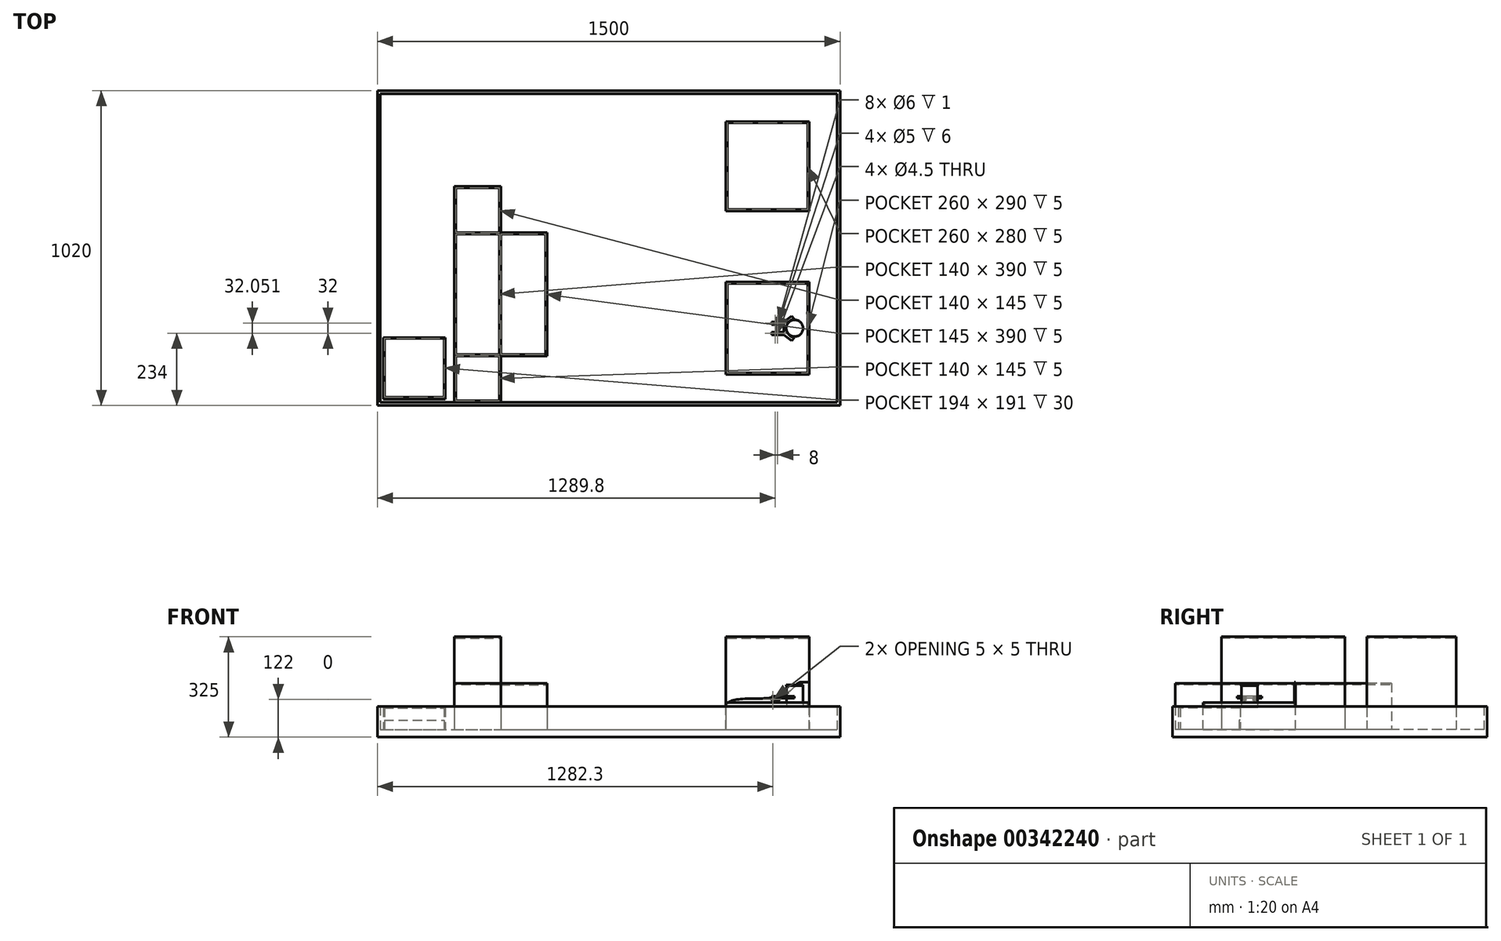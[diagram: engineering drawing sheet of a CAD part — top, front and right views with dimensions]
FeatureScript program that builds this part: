
annotation { "Feature Type Name" : "Feature", "Feature Type Description" : "" }
export const myFeature = defineFeature(function(context is Context, id is Id, definition is map)
    precondition{}
    {
        {
            var Q0;
            Q0=qCreatedBy(makeId("Top.planeOp"),FACE);
            var sketch = newSketch(context, id + "F0", { "sketchPlane" : qUnion([Q0])});
            skCircle(sketch, "E0", {"center": v(0, 0) * mm, "radius": 27.2 * mm});
            skSolve(sketch);
        }
        {
            var Q0;
            Q0=qSketchRegion(id+"F0",true);
            extrude(context, id + "F1", {"entities" : qUnion([Q0]), "depth" : 2.83 * mm});
        }
        {
            var Q0;
            Q0=makeQuery(id+"F1.opExtrude","CAP_FACE",FACE,{"disambiguationData":[OSD([sQuery(id+"F0.wireOp",EDGE,"E0")])],"isStart":false});
            var sketch = newSketch(context, id + "F2", { "sketchPlane" : qUnion([Q0])});
            skCircle(sketch, "E1", {"center": v(0, 0) * mm, "radius": 26.4 * mm});
            skSolve(sketch);
        }
        {
            var Q0;
            Q0=qSketchRegion(id+"F2",true);
            extrude(context, id + "F3", {"entities" : qUnion([Q0]), "operationType" : NewBodyOperationType.ADD, "depth" : 67.36 * mm});
        }
        {
            var Q0;
            Q0=makeQuery(id+"F3.opExtrude","CAP_FACE",FACE,{"disambiguationData":[OSD([sQuery(id+"F2.wireOp",EDGE,"E1")])],"isStart":false});
            var sketch = newSketch(context, id + "F4", { "sketchPlane" : qUnion([Q0])});
            skCircle(sketch, "E2", {"center": v(0, 0) * mm, "radius": 27.2 * mm});
            skSolve(sketch);
        }
        {
            var Q0;
            Q0=qSketchRegion(id+"F4",true);
            extrude(context, id + "F5", {"entities" : qUnion([Q0]), "operationType" : NewBodyOperationType.ADD, "depth" : 2.83 * mm});
        }
        {
            var Q0;
            Q0=makeQuery(id+"F5.opExtrude","CAP_FACE",FACE,{"disambiguationData":[OSD([sQuery(id+"F4.wireOp",EDGE,"E2")])],"isStart":false});
            var sketch = newSketch(context, id + "F6", { "sketchPlane" : qUnion([Q0])});
            skSolve(sketch);
        }
        {
            var Q0;
            Q0=qCreatedBy(makeId("Top.planeOp"),FACE);
            cPlane(context, id + "F7", {"entities" : qUnion([Q0]), "cplaneType" : CPlaneType.OFFSET, "offset" : 25 * mm, "width" : 150 * mm, "height" : 150 * mm});
        }
        {
            var Q0;
            Q0=makeQuery(id+"F6.imprint","IMPRINT",FACE,{"disambiguationData":[TD([[makeQuery(id+"F6.imprint","IMPRINT",EDGE,{"derivedFrom":makeQuery(id+"F5.opExtrude","CAP_EDGE",EDGE,{"disambiguationData":[OSD([sQuery(id+"F4.wireOp",EDGE,"E2")])],"isStart":false})}),1.0]])]});
            var sketch = newSketch(context, id + "F8", { "sketchPlane" : qUnion([Q0])});
            skSolve(sketch);
        }
        {
            var Q0;
            Q0=qCreatedBy(makeId("Top.planeOp"),FACE);
            var sketch = newSketch(context, id + "F9", { "sketchPlane" : qUnion([Q0])});
            skLineSegment(sketch, "E3.bottom", {"start": v(-222.8, -150) * mm, "end": v(47.2, -150) * mm});
            skLineSegment(sketch, "E3.top", {"start": v(-222.8, 150) * mm, "end": v(47.2, 150) * mm});
            skLineSegment(sketch, "E3.left", {"start": v(-222.8, -150) * mm, "end": v(-222.8, 150) * mm});
            skLineSegment(sketch, "E3.right", {"start": v(47.2, -150) * mm, "end": v(47.2, 150) * mm});
            skSolve(sketch);
        }
        {
            var Q0;
            Q0=qSketchRegion(id+"F9",true);
            extrude(context, id + "F10", {"entities" : qUnion([Q0]), "oppositeDirection" : true, "depth" : 72 * mm});
        }
        {
            var Q0;
            Q0=makeQuery(id+"F10.opExtrude","CAP_FACE",FACE,{"disambiguationData":[OSD([sQuery(id+"F9.wireOp",EDGE,"E3.bottom"),sQuery(id+"F9.wireOp",EDGE,"E3.top"),sQuery(id+"F9.wireOp",EDGE,"E3.left"),sQuery(id+"F9.wireOp",EDGE,"E3.right")])],"isStart":true});
            var sketch = newSketch(context, id + "F11", { "sketchPlane" : qUnion([Q0])});
            skLineSegment(sketch, "E4.bottom", {"start": v(-222.8, -150) * mm, "end": v(47.2, -150) * mm});
            skLineSegment(sketch, "E4.top", {"start": v(-222.8, -145) * mm, "end": v(42.2, -145) * mm});
            skLineSegment(sketch, "E4.left", {"start": v(-222.8, -150) * mm, "end": v(-222.8, -145) * mm});
            skLineSegment(sketch, "E5.bottom", {"start": v(47.2, 150) * mm, "end": v(42.2, 150) * mm});
            skLineSegment(sketch, "E5.left", {"start": v(47.2, 150) * mm, "end": v(47.2, -150) * mm});
            skLineSegment(sketch, "E5.right", {"start": v(42.2, 150) * mm, "end": v(42.2, -145) * mm});
            skSolve(sketch);
        }
        {
            var Q0;
            Q0=qSketchRegion(id+"F11",true);
            extrude(context, id + "F12", {"entities" : qUnion([Q0]), "operationType" : NewBodyOperationType.ADD, "depth" : 15 * mm});
        }
        {
            var Q0;
            Q0=makeQuery(id+"F12.boolean.opBoolean","MERGE",FACE,{"derivedFrom":[makeQuery(id+"F10.opExtrude","SWEPT_FACE",FACE,{"disambiguationData":[OSD([sQuery(id+"F9.wireOp",EDGE,"E3.top")])]}),makeQuery(id+"F12.opExtrude","SWEPT_FACE",FACE,{"disambiguationData":[OSD([sQuery(id+"F11.wireOp",EDGE,"E5.bottom")])]})]});
            var sketch = newSketch(context, id + "F13", { "sketchPlane" : qUnion([Q0])});
            skLineSegment(sketch, "E6", {"start": v(-47.2, 81.36) * mm, "end": v(-21.31, 81.36) * mm});
            skFitSpline(sketch, "E7", {"points": [v(-21.31, 81.36) * mm, v(15.24, 52.01) * mm, v(114.14, 28.17) * mm, v(222.8, 0) * mm], "startDerivative": vector(181.02, 0.3) * mm, "endDerivative": vector(-1.73, -239.85) * mm});
            skLineSegment(sketch, "E8", {"start": v(-47.2, 81.36) * mm, "end": v(-47.2, -72) * mm});
            skLineSegment(sketch, "E9", {"start": v(-47.2, -72) * mm, "end": v(222.8, -72) * mm});
            skLineSegment(sketch, "E10", {"start": v(222.8, -72) * mm, "end": v(222.8, 0) * mm});
            skSolve(sketch);
        }
        {
            var Q0;
            Q0=qSketchRegion(id+"F13",true);
            extrude(context, id + "F14", {"entities" : qUnion([Q0]), "operationType" : NewBodyOperationType.ADD, "oppositeDirection" : true, "depth" : 5 * mm});
        }
        {
            var Q0;
            Q0=makeQuery(id+"F10.opExtrude","CAP_FACE",FACE,{"disambiguationData":[OSD([sQuery(id+"F9.wireOp",EDGE,"E3.bottom"),sQuery(id+"F9.wireOp",EDGE,"E3.top"),sQuery(id+"F9.wireOp",EDGE,"E3.left"),sQuery(id+"F9.wireOp",EDGE,"E3.right")])],"isStart":true});
            var sketch = newSketch(context, id + "F15", { "sketchPlane" : qUnion([Q0])});
            skLineSegment(sketch, "E11.bottom", {"start": v(-222.8, 145) * mm, "end": v(-217.8, 145) * mm});
            skLineSegment(sketch, "E11.top", {"start": v(-222.8, -145) * mm, "end": v(-217.8, -145) * mm});
            skLineSegment(sketch, "E11.left", {"start": v(-222.8, 145) * mm, "end": v(-222.8, -145) * mm});
            skLineSegment(sketch, "E11.right", {"start": v(-217.8, 145) * mm, "end": v(-217.8, -145) * mm});
            skSolve(sketch);
        }
        {
            var Q0;
            Q0=qSketchRegion(id+"F15",true);
            extrude(context, id + "F16", {"entities" : qUnion([Q0]), "operationType" : NewBodyOperationType.ADD, "depth" : 5 * mm});
        }
        {
            var Q0;
            Q0=makeQuery(id+"F10.opExtrude","CAP_FACE",FACE,{"disambiguationData":[OSD([sQuery(id+"F9.wireOp",EDGE,"E3.bottom"),sQuery(id+"F9.wireOp",EDGE,"E3.top"),sQuery(id+"F9.wireOp",EDGE,"E3.left"),sQuery(id+"F9.wireOp",EDGE,"E3.right")])],"isStart":false});
            var sketch = newSketch(context, id + "F17", { "sketchPlane" : qUnion([Q0])});
            skLineSegment(sketch, "E12.bottom", {"start": v(147.2, 250) * mm, "end": v(-1352.8, 250) * mm});
            skLineSegment(sketch, "E12.top", {"start": v(147.2, -770) * mm, "end": v(-1352.8, -770) * mm});
            skLineSegment(sketch, "E12.left", {"start": v(147.2, 250) * mm, "end": v(147.2, -770) * mm});
            skLineSegment(sketch, "E12.right", {"start": v(-1352.8, 250) * mm, "end": v(-1352.8, -770) * mm});
            skSolve(sketch);
        }
        {
            var Q0;
            Q0=qSketchRegion(id+"F17",true);
            extrude(context, id + "F18", {"entities" : qUnion([Q0]), "operationType" : NewBodyOperationType.ADD, "depth" : 25 * mm});
        }
        {
            var Q0;
            Q0=makeQuery(id+"F18.opExtrude","CAP_FACE",FACE,{"disambiguationData":[OSD([sQuery(id+"F17.wireOp",EDGE,"E12.bottom"),sQuery(id+"F17.wireOp",EDGE,"E12.top"),sQuery(id+"F17.wireOp",EDGE,"E12.left"),sQuery(id+"F17.wireOp",EDGE,"E12.right")])],"isStart":true});
            var sketch = newSketch(context, id + "F19", { "sketchPlane" : qUnion([Q0])});
            skLineSegment(sketch, "E13.bottom", {"start": v(-222.8, 670) * mm, "end": v(47.2, 670) * mm});
            skLineSegment(sketch, "E13.top", {"start": v(-222.8, 380) * mm, "end": v(47.2, 380) * mm});
            skLineSegment(sketch, "E13.left", {"start": v(-222.8, 670) * mm, "end": v(-222.8, 380) * mm});
            skLineSegment(sketch, "E13.right", {"start": v(47.2, 670) * mm, "end": v(47.2, 380) * mm});
            skSolve(sketch);
        }
        {
            var Q0;
            Q0=qSketchRegion(id+"F19",true);
            extrude(context, id + "F20", {"entities" : qUnion([Q0]), "operationType" : NewBodyOperationType.ADD, "depth" : 300 * mm});
        }
        {
            var Q0;
            Q0=makeQuery(id+"F20.opExtrude","CAP_FACE",FACE,{"disambiguationData":[OSD([sQuery(id+"F19.wireOp",EDGE,"E13.bottom"),sQuery(id+"F19.wireOp",EDGE,"E13.top"),sQuery(id+"F19.wireOp",EDGE,"E13.left"),sQuery(id+"F19.wireOp",EDGE,"E13.right")])],"isStart":false});
            var sketch = newSketch(context, id + "F21", { "sketchPlane" : qUnion([Q0])});
            skLineSegment(sketch, "E14.bottom", {"start": v(-217.8, 665) * mm, "end": v(42.2, 665) * mm});
            skLineSegment(sketch, "E14.top", {"start": v(-217.8, 385) * mm, "end": v(42.2, 385) * mm});
            skLineSegment(sketch, "E14.left", {"start": v(-217.8, 665) * mm, "end": v(-217.8, 385) * mm});
            skLineSegment(sketch, "E14.right", {"start": v(42.2, 665) * mm, "end": v(42.2, 385) * mm});
            skSolve(sketch);
        }
        {
            var Q0;
            Q0=qSketchRegion(id+"F21",true);
            extrude(context, id + "F22", {"entities" : qUnion([Q0]), "operationType" : NewBodyOperationType.REMOVE, "oppositeDirection" : true, "depth" : 5 * mm});
        }
        {
            var Q0;
            Q0=makeQuery(id+"F18.opExtrude","CAP_FACE",FACE,{"disambiguationData":[OSD([sQuery(id+"F17.wireOp",EDGE,"E12.bottom"),sQuery(id+"F17.wireOp",EDGE,"E12.top"),sQuery(id+"F17.wireOp",EDGE,"E12.left"),sQuery(id+"F17.wireOp",EDGE,"E12.right")])],"isStart":true});
            var sketch = newSketch(context, id + "F23", { "sketchPlane" : qUnion([Q0])});
            skLineSegment(sketch, "E15.bottom", {"start": v(-1352.8, 770) * mm, "end": v(147.2, 770) * mm});
            skLineSegment(sketch, "E15.top", {"start": v(-1352.8, -250) * mm, "end": v(147.2, -250) * mm});
            skLineSegment(sketch, "E15.left", {"start": v(-1352.8, 770) * mm, "end": v(-1352.8, -250) * mm});
            skLineSegment(sketch, "E15.right", {"start": v(147.2, 770) * mm, "end": v(147.2, -250) * mm});
            skLineSegment(sketch, "E16.bottom", {"start": v(-1342.8, 760) * mm, "end": v(137.2, 760) * mm});
            skLineSegment(sketch, "E16.top", {"start": v(-1342.8, -240) * mm, "end": v(137.2, -240) * mm});
            skLineSegment(sketch, "E16.left", {"start": v(-1342.8, 760) * mm, "end": v(-1342.8, -240) * mm});
            skLineSegment(sketch, "E16.right", {"start": v(137.2, 760) * mm, "end": v(137.2, -240) * mm});
            skSolve(sketch);
        }
        {
            var Q0;
            Q0=qSketchRegion(id+"F23",true);
            extrude(context, id + "F24", {"entities" : qUnion([Q0]), "operationType" : NewBodyOperationType.ADD, "depth" : 75 * mm});
        }
        {
            var Q0;
            Q0=makeQuery(id+"F18.opExtrude","CAP_FACE",FACE,{"disambiguationData":[OSD([sQuery(id+"F17.wireOp",EDGE,"E12.bottom"),sQuery(id+"F17.wireOp",EDGE,"E12.top"),sQuery(id+"F17.wireOp",EDGE,"E12.left"),sQuery(id+"F17.wireOp",EDGE,"E12.right")])],"isStart":true});
            var sketch = newSketch(context, id + "F25", { "sketchPlane" : qUnion([Q0])});
            skLineSegment(sketch, "E17.bottom", {"start": v(-1102.8, 460) * mm, "end": v(-952.8, 460) * mm});
            skLineSegment(sketch, "E17.top", {"start": v(-1102.8, -240) * mm, "end": v(-952.8, -240) * mm});
            skLineSegment(sketch, "E17.left", {"start": v(-1102.8, 460) * mm, "end": v(-1102.8, -240) * mm});
            skLineSegment(sketch, "E17.right", {"start": v(-952.8, 460) * mm, "end": v(-952.8, 310) * mm});
            skLineSegment(sketch, "E18.bottom", {"start": v(-952.8, 310) * mm, "end": v(-802.8, 310) * mm});
            skLineSegment(sketch, "E18.top", {"start": v(-952.8, -90) * mm, "end": v(-802.8, -90) * mm});
            skLineSegment(sketch, "E18.right", {"start": v(-802.8, 310) * mm, "end": v(-802.8, -90) * mm});
            skLineSegment(sketch, "E19.trimOffspring", {"start": v(-952.8, -90) * mm, "end": v(-952.8, -240) * mm});
            skSolve(sketch);
        }
        {
            var Q0;
            Q0=qSketchRegion(id+"F25",true);
            extrude(context, id + "F26", {"entities" : qUnion([Q0]), "operationType" : NewBodyOperationType.ADD, "depth" : 150 * mm});
        }
        {
            var Q0;
            Q0=makeQuery(id+"F26.opExtrude","CAP_FACE",FACE,{"disambiguationData":[OSD([sQuery(id+"F25.wireOp",EDGE,"E17.bottom"),sQuery(id+"F25.wireOp",EDGE,"E17.top"),sQuery(id+"F25.wireOp",EDGE,"E17.left"),sQuery(id+"F25.wireOp",EDGE,"E17.right"),sQuery(id+"F25.wireOp",EDGE,"E18.bottom"),sQuery(id+"F25.wireOp",EDGE,"E18.top"),sQuery(id+"F25.wireOp",EDGE,"E18.right"),sQuery(id+"F25.wireOp",EDGE,"E19.trimOffspring")])],"isStart":false});
            var sketch = newSketch(context, id + "F27", { "sketchPlane" : qUnion([Q0])});
            skLineSegment(sketch, "E20.bottom", {"start": v(-952.8, 310) * mm, "end": v(-1102.8, 310) * mm});
            skLineSegment(sketch, "E20.top", {"start": v(-952.8, -90) * mm, "end": v(-1102.8, -90) * mm});
            skLineSegment(sketch, "E20.left", {"start": v(-952.8, 310) * mm, "end": v(-952.8, -90) * mm});
            skLineSegment(sketch, "E20.right", {"start": v(-1102.8, 310) * mm, "end": v(-1102.8, -90) * mm});
            skSolve(sketch);
        }
        {
            var Q0;
            Q0=qSketchRegion(id+"F27",true);
            extrude(context, id + "F28", {"entities" : qUnion([Q0]), "operationType" : NewBodyOperationType.ADD, "depth" : 150 * mm});
        }
        {
            var Q0;
            Q0=makeQuery(id+"F28.opExtrude","CAP_FACE",FACE,{"disambiguationData":[OSD([sQuery(id+"F27.wireOp",EDGE,"E20.bottom"),sQuery(id+"F27.wireOp",EDGE,"E20.top"),sQuery(id+"F27.wireOp",EDGE,"E20.left"),sQuery(id+"F27.wireOp",EDGE,"E20.right")])],"isStart":false});
            var sketch = newSketch(context, id + "F29", { "sketchPlane" : qUnion([Q0])});
            skLineSegment(sketch, "E21.bottom", {"start": v(-1097.8, 305) * mm, "end": v(-957.8, 305) * mm});
            skLineSegment(sketch, "E21.top", {"start": v(-1097.8, -85) * mm, "end": v(-957.8, -85) * mm});
            skLineSegment(sketch, "E21.left", {"start": v(-1097.8, 305) * mm, "end": v(-1097.8, -85) * mm});
            skLineSegment(sketch, "E21.right", {"start": v(-957.8, 305) * mm, "end": v(-957.8, -85) * mm});
            skSolve(sketch);
        }
        {
            var Q0;
            Q0=qSketchRegion(id+"F29",true);
            extrude(context, id + "F30", {"entities" : qUnion([Q0]), "operationType" : NewBodyOperationType.REMOVE, "oppositeDirection" : true, "depth" : 5 * mm});
        }
        {
            var Q0;
            {var subQ0=sQuery(id+"F25.wireOp",EDGE,"E17.left");var subQ1=sQuery(id+"F25.wireOp",EDGE,"E18.bottom");var subQ2=sQuery(id+"F25.wireOp",EDGE,"E17.right");var subQ3=sQuery(id+"F25.wireOp",EDGE,"E17.bottom");var subQ4=makeQuery(id+"F26.opExtrude","CAP_FACE",FACE,{"disambiguationData":[OSD([subQ3,sQuery(id+"F25.wireOp",EDGE,"E17.top"),subQ0,subQ2,subQ1,sQuery(id+"F25.wireOp",EDGE,"E18.top"),sQuery(id+"F25.wireOp",EDGE,"E18.right"),sQuery(id+"F25.wireOp",EDGE,"E19.trimOffspring")])],"isStart":false});Q0=makeQuery(id+"F28.boolean.opBoolean","SPLIT",FACE,{"disambiguationData":[TD([makeQuery(id+"F26.opExtrude","SWEPT_FACE",FACE,{"disambiguationData":[OSD([subQ3])]})])],"derivedFrom":subQ4});}
            var sketch = newSketch(context, id + "F31", { "sketchPlane" : qUnion([Q0])});
            skLineSegment(sketch, "E22.bottom", {"start": v(-1097.8, 455) * mm, "end": v(-957.8, 455) * mm});
            skLineSegment(sketch, "E22.top", {"start": v(-1097.8, 310) * mm, "end": v(-957.8, 310) * mm});
            skLineSegment(sketch, "E22.left", {"start": v(-1097.8, 455) * mm, "end": v(-1097.8, 310) * mm});
            skLineSegment(sketch, "E22.right", {"start": v(-957.8, 455) * mm, "end": v(-957.8, 310) * mm});
            skLineSegment(sketch, "E23.bottom", {"start": v(-952.8, 305) * mm, "end": v(-807.8, 305) * mm});
            skLineSegment(sketch, "E23.top", {"start": v(-952.8, -85) * mm, "end": v(-807.8, -85) * mm});
            skLineSegment(sketch, "E23.left", {"start": v(-952.8, 305) * mm, "end": v(-952.8, -85) * mm});
            skLineSegment(sketch, "E23.right", {"start": v(-807.8, 305) * mm, "end": v(-807.8, -85) * mm});
            skLineSegment(sketch, "E24.bottom", {"start": v(-1097.8, -90) * mm, "end": v(-957.8, -90) * mm});
            skLineSegment(sketch, "E24.top", {"start": v(-1097.8, -235) * mm, "end": v(-957.8, -235) * mm});
            skLineSegment(sketch, "E24.left", {"start": v(-1097.8, -90) * mm, "end": v(-1097.8, -235) * mm});
            skLineSegment(sketch, "E24.right", {"start": v(-957.8, -90) * mm, "end": v(-957.8, -235) * mm});
            skSolve(sketch);
        }
        {
            var Q0;
            Q0=qSketchRegion(id+"F31",true);
            extrude(context, id + "F32", {"entities" : qUnion([Q0]), "operationType" : NewBodyOperationType.REMOVE, "oppositeDirection" : true, "depth" : 5 * mm});
        }
        {
            var Q0;
            Q0=qCreatedBy(id+"F7.planeOp",FACE);
            var sketch = newSketch(context, id + "F33", { "sketchPlane" : qUnion([Q0])});
            skLineSegment(sketch, "E25", {"start": v(0, 0) * mm, "end": v(-90, 0) * mm, "construction": true});
            skLineSegment(sketch, "E26.bottom", {"start": v(-74.5, -12) * mm, "end": v(-55, -12) * mm});
            skLineSegment(sketch, "E26.top", {"start": v(-74.5, -20) * mm, "end": v(-55, -20) * mm});
            skLineSegment(sketch, "E26.left", {"start": v(-74.5, -12) * mm, "end": v(-74.5, -13) * mm});
            skPoint(sketch, "E27.visualSharp", {"position": v(-51, -12) * mm});
            skPoint(sketch, "E28.visualSharp", {"position": v(-51, -20) * mm});
            skCircle(sketch, "E29", {"center": v(-55, -16) * mm, "radius": 3 * mm});
            skLineSegment(sketch, "E30", {"start": v(-59, -3.98) * mm, "end": v(-59, -18.08) * mm, "construction": true});
            skCircle(sketch, "E31.MirrorC", {"center": v(-63, -16) * mm, "radius": 3 * mm});
            skLineSegment(sketch, "E32.bottom", {"start": v(-74.5, -13) * mm, "end": v(-65.65, -13) * mm});
            skLineSegment(sketch, "E32.top", {"start": v(-74.5, -19) * mm, "end": v(-65.65, -19) * mm});
            skArc(sketch, "E33", {"start": v(-65.65, -13) * mm, "mid": v(-67, -16) * mm, "end": v(-65.65, -19) * mm});
            skLineSegment(sketch, "E34.trimOffspring", {"start": v(-74.5, -19) * mm, "end": v(-74.5, -20) * mm});
            skArc(sketch, "E35.trimOffspring", {"start": v(-55, -20) * mm, "mid": v(-51, -16) * mm, "end": v(-55, -12) * mm});
            skLineSegment(sketch, "E36.MirrorCS", {"start": v(-74.5, 12) * mm, "end": v(-74.5, 13) * mm});
            skLineSegment(sketch, "E37.MirrorCS", {"start": v(-74.5, 19) * mm, "end": v(-74.5, 20) * mm});
            skPoint(sketch, "E38.MirrorP", {"position": v(-51, 12) * mm});
            skLineSegment(sketch, "E39.MirrorCS", {"start": v(-74.5, 12) * mm, "end": v(-55, 12) * mm});
            skPoint(sketch, "E40.MirrorP", {"position": v(-51, 20) * mm});
            skArc(sketch, "E41.MirrorCS", {"start": v(-65.65, 13) * mm, "mid": v(-67, 16) * mm, "end": v(-65.65, 19) * mm});
            skArc(sketch, "E42.MirrorCS", {"start": v(-55, 20) * mm, "mid": v(-51, 16) * mm, "end": v(-55, 12) * mm});
            skLineSegment(sketch, "E43.MirrorCS", {"start": v(-74.5, 20) * mm, "end": v(-55, 20) * mm});
            skCircle(sketch, "E44.MirrorC", {"center": v(-55, 16) * mm, "radius": 3 * mm});
            skCircle(sketch, "E45.MirrorC", {"center": v(-63, 16) * mm, "radius": 3 * mm});
            skLineSegment(sketch, "E46.MirrorCS", {"start": v(-74.5, 19) * mm, "end": v(-65.65, 19) * mm});
            skLineSegment(sketch, "E47.MirrorCS", {"start": v(-74.5, 13) * mm, "end": v(-65.65, 13) * mm});
            skSolve(sketch);
        }
        {
            var Q0;
            Q0=qSketchRegion(id+"F33",true);
            var Q1;
            Q1=qSketchRegion(id+"F36",true);
            extrude(context, id + "F34", {"entities" : qUnion([Q0, Q1]), "depth" : 8 * mm, "symmetric" : true});
        }
        {
            var Q0;
            Q0=makeQuery(id+"F34.opExtrude","CAP_EDGE",EDGE,{"disambiguationData":[OSD([sQuery(id+"F33.wireOp",EDGE,"E34.trimOffspring")])],"isStart":false});
            var Q1;
            Q1=makeQuery(id+"F34.opExtrude","CAP_EDGE",EDGE,{"disambiguationData":[OSD([sQuery(id+"F33.wireOp",EDGE,"E26.left")])],"isStart":false});
            var Q2;
            Q2=makeQuery(id+"F34.opExtrude","CAP_EDGE",EDGE,{"disambiguationData":[OSD([sQuery(id+"F33.wireOp",EDGE,"E34.trimOffspring")])],"isStart":true});
            var Q3;
            Q3=makeQuery(id+"F34.opExtrude","CAP_EDGE",EDGE,{"disambiguationData":[OSD([sQuery(id+"F33.wireOp",EDGE,"E26.left")])],"isStart":true});
            var Q4;
            Q4=makeQuery(id+"F34.opExtrude","CAP_EDGE",EDGE,{"disambiguationData":[OSD([sQuery(id+"F33.wireOp",EDGE,"E36.MirrorCS")])],"isStart":false});
            var Q5;
            Q5=makeQuery(id+"F34.opExtrude","CAP_EDGE",EDGE,{"disambiguationData":[OSD([sQuery(id+"F33.wireOp",EDGE,"E37.MirrorCS")])],"isStart":false});
            var Q6;
            Q6=makeQuery(id+"F34.opExtrude","CAP_EDGE",EDGE,{"disambiguationData":[OSD([sQuery(id+"F33.wireOp",EDGE,"E37.MirrorCS")])],"isStart":true});
            var Q7;
            Q7=makeQuery(id+"F34.opExtrude","CAP_EDGE",EDGE,{"disambiguationData":[OSD([sQuery(id+"F33.wireOp",EDGE,"E36.MirrorCS")])],"isStart":true});
            fillet(context, id + "F35", {"entities" : qUnion([Q0, Q1, Q2, Q3, Q4, Q5, Q6, Q7]), "radius" : 4 * mm, "tangentPropagation" : true, "allowEdgeOverflow" : false});
        }
        {
            var Q0;
            Q0=makeQuery(id+"F34.opExtrude","SWEPT_FACE",FACE,{"disambiguationData":[OSD([sQuery(id+"F33.wireOp",EDGE,"E26.top")])]});
            var sketch = newSketch(context, id + "F36", { "sketchPlane" : qUnion([Q0])});
            skCircle(sketch, "E48", {"center": v(-70.5, 25) * mm, "radius": 3 * mm});
            skSolve(sketch);
        }
        {
            var Q0;
            Q0=qSketchRegion(id+"F36",true);
            var Q1;
            Q1=makeQuery(id+"F34.opExtrude","SWEPT_FACE",FACE,{"disambiguationData":[OSD([sQuery(id+"F33.wireOp",EDGE,"E26.bottom")])]});
            extrude(context, id + "F37", {"entities" : qUnion([Q0]), "operationType" : NewBodyOperationType.ADD, "endBound" : BoundingType.UP_TO_SURFACE, "oppositeDirection" : true, "endBoundEntityFace" : qUnion([Q1]), "depth" : 25 * mm});
        }
        {
            var Q0;
            Q0=makeQuery(id+"F34.opExtrude","SWEPT_FACE",FACE,{"disambiguationData":[OSD([sQuery(id+"F33.wireOp",EDGE,"E43.MirrorCS")])]});
            var sketch = newSketch(context, id + "F38", { "sketchPlane" : qUnion([Q0])});
            skCircle(sketch, "E49", {"center": v(70.5, 25) * mm, "radius": 3 * mm});
            skSolve(sketch);
        }
        {
            var Q0;
            Q0=qSketchRegion(id+"F38",true);
            var Q1;
            Q1=makeQuery(id+"F34.opExtrude","SWEPT_FACE",FACE,{"disambiguationData":[OSD([sQuery(id+"F33.wireOp",EDGE,"E39.MirrorCS")])]});
            extrude(context, id + "F39", {"entities" : qUnion([Q0]), "operationType" : NewBodyOperationType.ADD, "endBound" : BoundingType.UP_TO_SURFACE, "oppositeDirection" : true, "endBoundEntityFace" : qUnion([Q1]), "depth" : 25 * mm});
        }
        {
            var Q0;
            Q0=qCreatedBy(id+"F7.planeOp",FACE);
            var sketch = newSketch(context, id + "F40", { "sketchPlane" : qUnion([Q0])});
            skCircle(sketch, "E50", {"center": v(-55, 16) * mm, "radius": 3 * mm});
            skCircle(sketch, "E51", {"center": v(-63, 16) * mm, "radius": 2.5 * mm});
            skCircle(sketch, "E52", {"center": v(-63, 16) * mm, "radius": 3 * mm});
            skCircle(sketch, "E53", {"center": v(-55, 16) * mm, "radius": 2.5 * mm});
            skSolve(sketch);
        }
        {
            var Q0;
            Q0=qSketchRegion(id+"F40",true);
            extrude(context, id + "F41", {"entities" : qUnion([Q0]), "operationType" : NewBodyOperationType.ADD, "depth" : 6 * mm, "symmetric" : true});
        }
        {
            var Q0;
            Q0=qCreatedBy(id+"F7.planeOp",FACE);
            var sketch = newSketch(context, id + "F42", { "sketchPlane" : qUnion([Q0])});
            skCircle(sketch, "E54", {"center": v(-63, -16) * mm, "radius": 2.5 * mm});
            skCircle(sketch, "E55", {"center": v(-63, -16) * mm, "radius": 3 * mm});
            skCircle(sketch, "E56", {"center": v(-55, -16) * mm, "radius": 2.5 * mm});
            skCircle(sketch, "E57", {"center": v(-55, -16) * mm, "radius": 3 * mm});
            skSolve(sketch);
        }
        {
            var Q0;
            Q0=qSketchRegion(id+"F42",true);
            extrude(context, id + "F43", {"entities" : qUnion([Q0]), "operationType" : NewBodyOperationType.ADD, "depth" : 6 * mm, "symmetric" : true});
        }
        {
            var Q0;
            Q0=makeQuery(id+"F34.opExtrude","SWEPT_FACE",FACE,{"disambiguationData":[OSD([sQuery(id+"F33.wireOp",EDGE,"E43.MirrorCS")])]});
            var sketch = newSketch(context, id + "F44", { "sketchPlane" : qUnion([Q0])});
            skArc(sketch, "E58", {"start": v(71.5, 27.3) * mm, "mid": v(70.5, 27.5) * mm, "end": v(69.5, 27.3) * mm});
            skLineSegment(sketch, "E59.bottom", {"start": v(68.2, 26) * mm, "end": v(69.5, 26) * mm});
            skLineSegment(sketch, "E59.top", {"start": v(68.2, 24) * mm, "end": v(69.5, 24) * mm});
            skLineSegment(sketch, "E60.left", {"start": v(71.5, 27.3) * mm, "end": v(71.5, 26) * mm});
            skLineSegment(sketch, "E60.right", {"start": v(69.5, 27.3) * mm, "end": v(69.5, 26) * mm});
            skPoint(sketch, "E61.orphan", {"position": v(69.5, 27.8) * mm});
            skPoint(sketch, "E62.orphan", {"position": v(71.5, 27.8) * mm});
            skArc(sketch, "E63.trimOffspring", {"start": v(68.2, 26) * mm, "mid": v(68, 25) * mm, "end": v(68.2, 24) * mm});
            skPoint(sketch, "E59.left.start.orphan", {"position": v(67.32, 26) * mm});
            skPoint(sketch, "E64.orphan", {"position": v(67.32, 24) * mm});
            skArc(sketch, "E65.trimOffspring", {"start": v(69.5, 22.7) * mm, "mid": v(70.5, 22.5) * mm, "end": v(71.5, 22.7) * mm});
            skLineSegment(sketch, "E66.trimOffspring", {"start": v(69.5, 24) * mm, "end": v(69.5, 22.7) * mm});
            skLineSegment(sketch, "E67.trimOffspring", {"start": v(71.5, 26) * mm, "end": v(72.8, 26) * mm});
            skLineSegment(sketch, "E68.trimOffspring", {"start": v(71.5, 24) * mm, "end": v(71.5, 22.7) * mm});
            skLineSegment(sketch, "E69.trimOffspring", {"start": v(71.5, 24) * mm, "end": v(72.8, 24) * mm});
            skPoint(sketch, "E60.top.end.orphan", {"position": v(69.5, 22.2) * mm});
            skPoint(sketch, "E70.orphan", {"position": v(71.5, 22.2) * mm});
            skPoint(sketch, "E59.right.end.orphan", {"position": v(73.68, 24) * mm});
            skPoint(sketch, "E71.orphan", {"position": v(73.68, 26) * mm});
            skArc(sketch, "E72.trimOffspring", {"start": v(72.8, 24) * mm, "mid": v(73, 25) * mm, "end": v(72.8, 26) * mm});
            skSolve(sketch);
        }
        {
            var Q0;
            Q0=qSketchRegion(id+"F44",true);
            extrude(context, id + "F45", {"entities" : qUnion([Q0]), "operationType" : NewBodyOperationType.REMOVE, "endBound" : BoundingType.THROUGH_ALL, "oppositeDirection" : true, "depth" : 25 * mm});
        }
        {
            var Q0;
            Q0=makeQuery(id+"F18.opExtrude","CAP_FACE",FACE,{"disambiguationData":[OSD([sQuery(id+"F17.wireOp",EDGE,"E12.bottom"),sQuery(id+"F17.wireOp",EDGE,"E12.top"),sQuery(id+"F17.wireOp",EDGE,"E12.left"),sQuery(id+"F17.wireOp",EDGE,"E12.right")])],"isStart":true});
            var sketch = newSketch(context, id + "F46", { "sketchPlane" : qUnion([Q0])});
            skLineSegment(sketch, "E73.bottom", {"start": v(-1332.8, -30) * mm, "end": v(-1132.8, -30) * mm});
            skLineSegment(sketch, "E73.top", {"start": v(-1332.8, -230) * mm, "end": v(-1132.8, -230) * mm});
            skLineSegment(sketch, "E73.left", {"start": v(-1332.8, -30) * mm, "end": v(-1332.8, -230) * mm});
            skLineSegment(sketch, "E73.right", {"start": v(-1132.8, -30) * mm, "end": v(-1132.8, -230) * mm});
            skLineSegment(sketch, "E74.bottom", {"start": v(-1329.8, -33) * mm, "end": v(-1135.8, -33) * mm});
            skLineSegment(sketch, "E74.top", {"start": v(-1329.8, -224) * mm, "end": v(-1135.8, -224) * mm});
            skLineSegment(sketch, "E74.left", {"start": v(-1329.8, -33) * mm, "end": v(-1329.8, -224) * mm});
            skLineSegment(sketch, "E74.right", {"start": v(-1135.8, -33) * mm, "end": v(-1135.8, -224) * mm});
            skSolve(sketch);
        }
        {
            var Q0;
            Q0=qSketchRegion(id+"F46",true);
            extrude(context, id + "F47", {"entities" : qUnion([Q0]), "operationType" : NewBodyOperationType.ADD, "depth" : 30 * mm});
        }
        {
            var Q0;
            Q0=makeQuery(id+"F47.opExtrude","CAP_FACE",FACE,{"disambiguationData":[OSD([sQuery(id+"F46.wireOp",EDGE,"E73.bottom"),sQuery(id+"F46.wireOp",EDGE,"E73.top"),sQuery(id+"F46.wireOp",EDGE,"E73.left"),sQuery(id+"F46.wireOp",EDGE,"E73.right"),sQuery(id+"F46.wireOp",EDGE,"E74.bottom"),sQuery(id+"F46.wireOp",EDGE,"E74.top"),sQuery(id+"F46.wireOp",EDGE,"E74.left"),sQuery(id+"F46.wireOp",EDGE,"E74.right")])],"isStart":false});
            var sketch = newSketch(context, id + "F48", { "sketchPlane" : qUnion([Q0])});
            skLineSegment(sketch, "E75.bottom", {"start": v(-1332.8, -30) * mm, "end": v(-1329.8, -30) * mm});
            skLineSegment(sketch, "E75.top", {"start": v(-1332.8, -230) * mm, "end": v(-1329.8, -230) * mm});
            skLineSegment(sketch, "E75.left", {"start": v(-1332.8, -30) * mm, "end": v(-1332.8, -230) * mm});
            skLineSegment(sketch, "E75.right", {"start": v(-1329.8, -30) * mm, "end": v(-1329.8, -224) * mm});
            skLineSegment(sketch, "E76.bottom", {"start": v(-1329.8, -230) * mm, "end": v(-1135.8, -230) * mm});
            skLineSegment(sketch, "E76.top", {"start": v(-1329.8, -224) * mm, "end": v(-1135.8, -224) * mm});
            skLineSegment(sketch, "E77.bottom", {"start": v(-1135.8, -230) * mm, "end": v(-1132.8, -230) * mm});
            skLineSegment(sketch, "E77.top", {"start": v(-1135.8, -30) * mm, "end": v(-1132.8, -30) * mm});
            skLineSegment(sketch, "E77.left", {"start": v(-1135.8, -224) * mm, "end": v(-1135.8, -30) * mm});
            skLineSegment(sketch, "E77.right", {"start": v(-1132.8, -230) * mm, "end": v(-1132.8, -30) * mm});
            skSolve(sketch);
        }
        {
            var Q0;
            Q0=qSketchRegion(id+"F48",true);
            extrude(context, id + "F49", {"entities" : qUnion([Q0]), "operationType" : NewBodyOperationType.ADD, "depth" : 40 * mm});
        }
        {
            var Q0;
            Q0=makeQuery(id+"F34.opExtrude","CAP_FACE",FACE,{"disambiguationData":[OSD([sQuery(id+"F33.wireOp",EDGE,"E26.bottom"),sQuery(id+"F33.wireOp",EDGE,"E26.top"),sQuery(id+"F33.wireOp",EDGE,"E26.left"),sQuery(id+"F33.wireOp",EDGE,"E29"),sQuery(id+"F33.wireOp",EDGE,"E31.MirrorC"),sQuery(id+"F33.wireOp",EDGE,"E32.bottom"),sQuery(id+"F33.wireOp",EDGE,"E32.top"),sQuery(id+"F33.wireOp",EDGE,"E33"),sQuery(id+"F33.wireOp",EDGE,"E34.trimOffspring"),sQuery(id+"F33.wireOp",EDGE,"E35.trimOffspring")])],"isStart":false});
            var sketch = newSketch(context, id + "F50", { "sketchPlane" : qUnion([Q0])});
            skArc(sketch, "E78", {"start": v(-0.88, 29.65) * mm, "mid": v(-27.1, -0.17) * mm, "end": v(-0.87, -29.97) * mm});
            skLineSegment(sketch, "E79", {"start": v(-0.88, 29.65) * mm, "end": v(-10.4, 39.9) * mm});
            skLineSegment(sketch, "E80", {"start": v(-74.74, -21) * mm, "end": v(-34.74, -21) * mm});
            skLineSegment(sketch, "E81", {"start": v(-74.74, 20.7) * mm, "end": v(-34.74, 20.7) * mm});
            skLineSegment(sketch, "E82", {"start": v(-34.74, 20.7) * mm, "end": v(-10.4, 39.9) * mm});
            skLineSegment(sketch, "E83", {"start": v(-34.74, -21) * mm, "end": v(-10.4, -40.21) * mm});
            skLineSegment(sketch, "E84", {"start": v(-10.4, -40.21) * mm, "end": v(-0.87, -29.97) * mm});
            skLineSegment(sketch, "E85", {"start": v(-74.74, 20.7) * mm, "end": v(-74.74, 11.7) * mm});
            skLineSegment(sketch, "E86", {"start": v(-74.74, 11.7) * mm, "end": v(-34.74, 11.7) * mm});
            skLineSegment(sketch, "E87", {"start": v(-34.74, 11.7) * mm, "end": v(-34.74, -12) * mm});
            skLineSegment(sketch, "E88", {"start": v(-34.74, -12) * mm, "end": v(-74.74, -12) * mm});
            skLineSegment(sketch, "E89", {"start": v(-74.74, -12) * mm, "end": v(-74.74, -21) * mm});
            skCircle(sketch, "E90", {"center": v(-63, 16.01) * mm, "radius": 2.25 * mm});
            skCircle(sketch, "E91", {"center": v(-55.07, 16.05) * mm, "radius": 2.25 * mm});
            skCircle(sketch, "E92", {"center": v(-63, -16) * mm, "radius": 2.25 * mm});
            skCircle(sketch, "E93", {"center": v(-55, -16) * mm, "radius": 2.25 * mm});
            skSolve(sketch);
        }
        {
            var Q0;
            Q0 = qSketchRegion(id + "F50", true);
            extrude(context, id + "F51", {"entities" : qUnion([Q0]), "depth" : 6 * mm});
        }
    });
